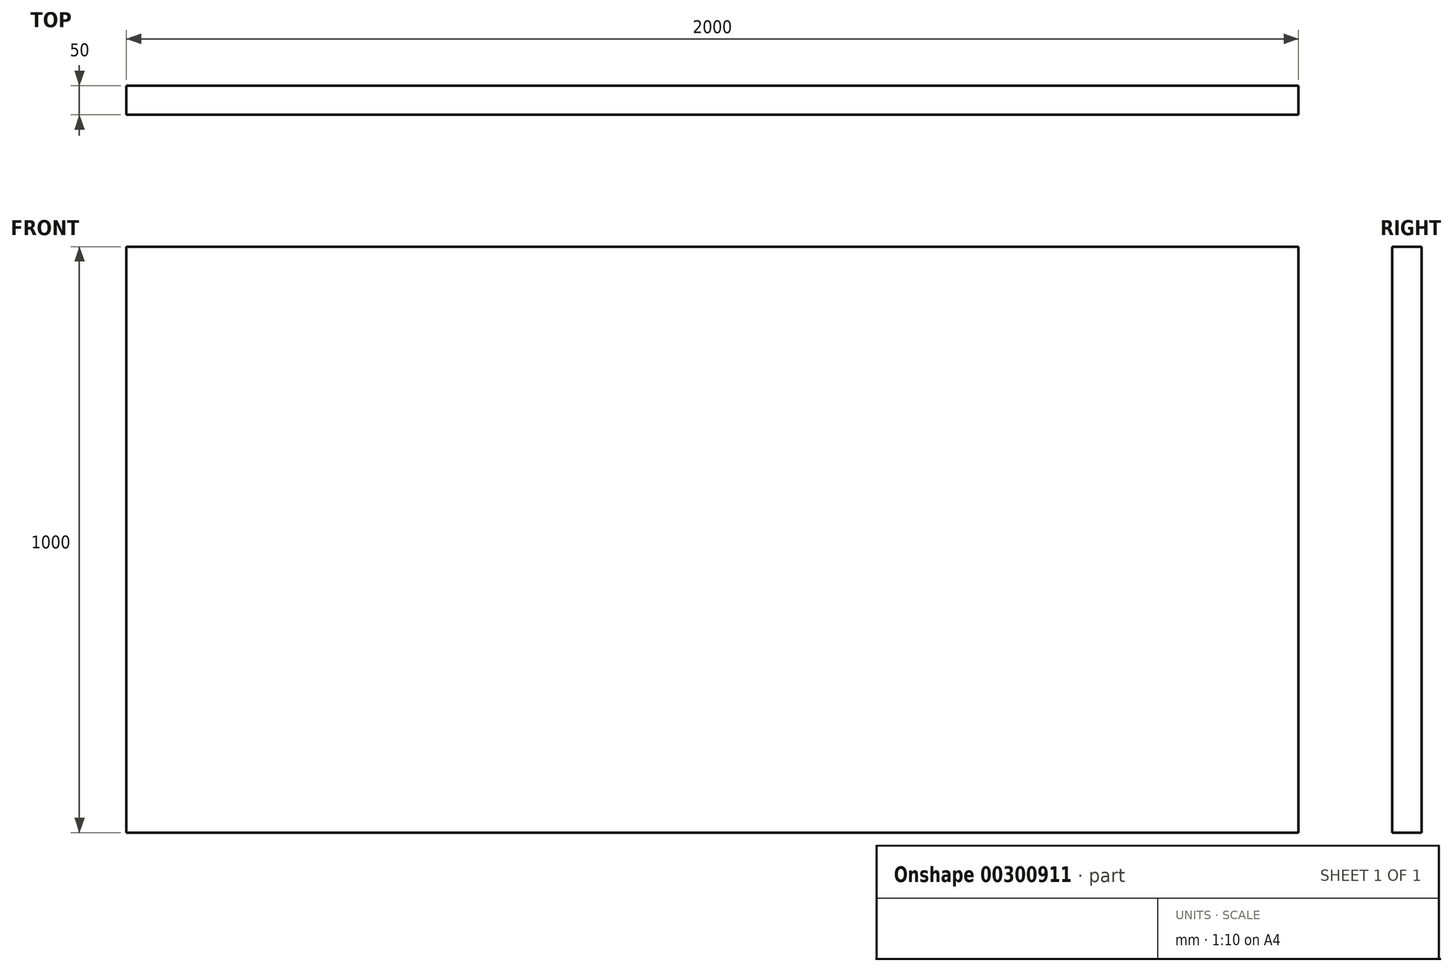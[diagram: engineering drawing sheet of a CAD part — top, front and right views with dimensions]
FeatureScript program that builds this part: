
annotation { "Feature Type Name" : "Feature", "Feature Type Description" : "" }
export const myFeature = defineFeature(function(context is Context, id is Id, definition is map)
    precondition{}
    {
        {
            var Q0;
            Q0=qCreatedBy(makeId("Front.planeOp"),FACE);
            var sketch = newSketch(context, id + "F0", { "sketchPlane" : qUnion([Q0])});
            skLineSegment(sketch, "E0.bottom", {"start": v(0, 0) * mm, "end": v(2000, 0) * mm});
            skLineSegment(sketch, "E0.top", {"start": v(0, 1000) * mm, "end": v(2000, 1000) * mm});
            skLineSegment(sketch, "E0.left", {"start": v(0, 0) * mm, "end": v(0, 1000) * mm});
            skLineSegment(sketch, "E0.right", {"start": v(2000, 0) * mm, "end": v(2000, 1000) * mm});
            skSolve(sketch);
        }
        {
            var Q0;
            Q0=makeQuery(id+"F0.imprint","IMPRINT",FACE,{"disambiguationData":[TD([[makeQuery(id+"F0.imprint","IMPRINT",EDGE,{"derivedFrom":sQuery(id+"F0.wireOp",EDGE,"E0.bottom")}),1.0]])]});
            extrude(context, id + "F1", {"entities" : qUnion([Q0]), "depth" : 50 * mm});
        }
    });
